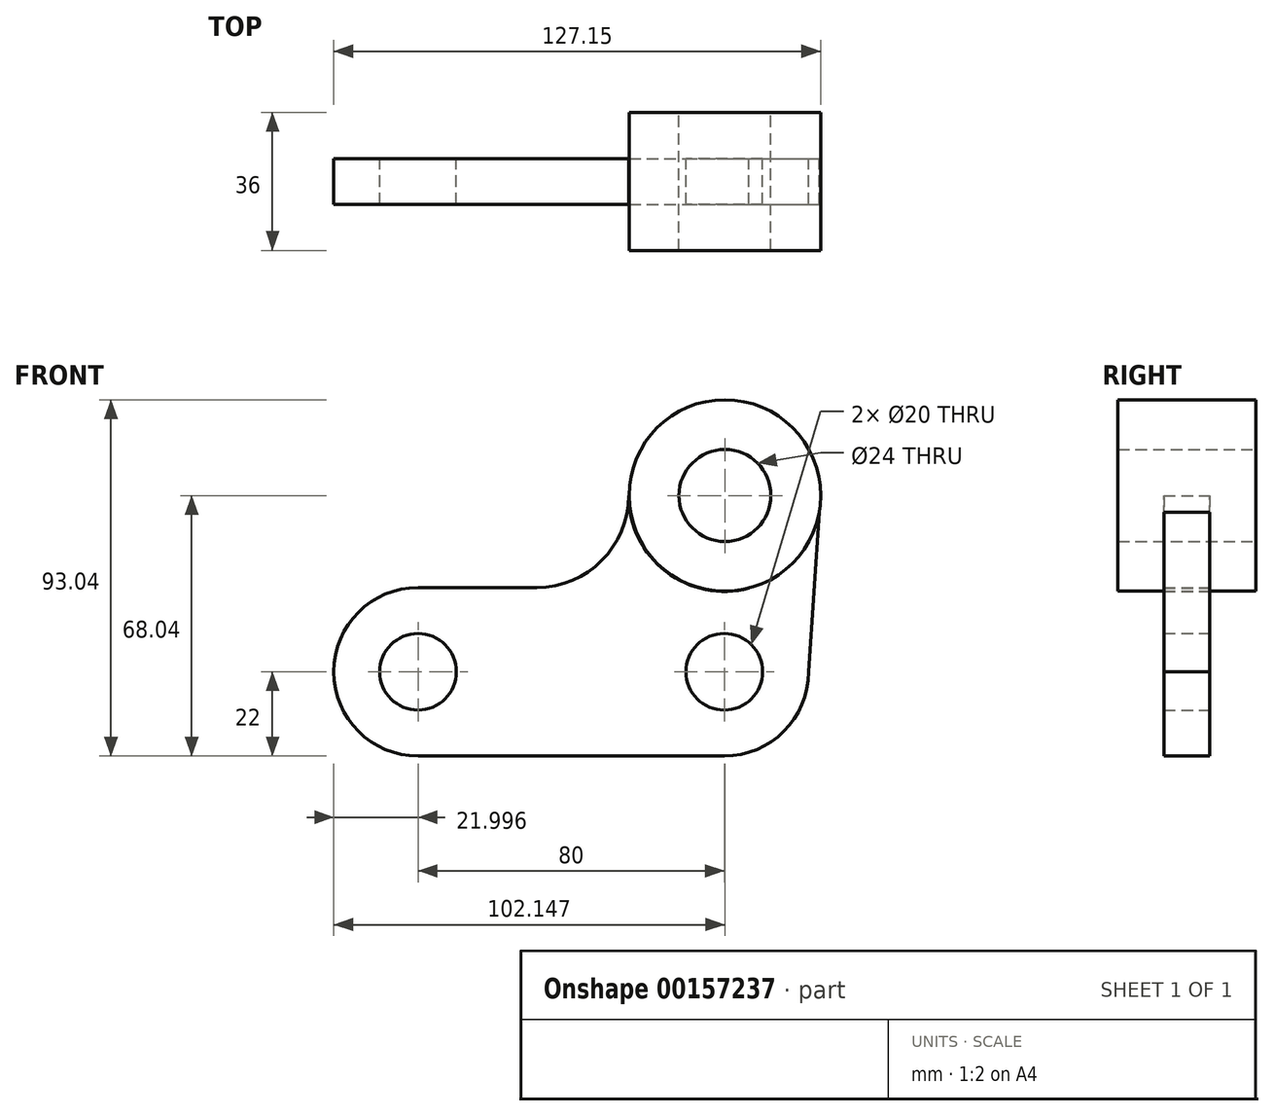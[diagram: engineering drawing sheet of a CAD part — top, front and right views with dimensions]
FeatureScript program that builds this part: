
annotation { "Feature Type Name" : "Feature", "Feature Type Description" : "" }
export const myFeature = defineFeature(function(context is Context, id is Id, definition is map)
    precondition{}
    {
        {
            var Q0;
            Q0=qCreatedBy(makeId("Front.planeOp"),FACE);
            var sketch = newSketch(context, id + "F0", { "sketchPlane" : qUnion([Q0])});
            skLineSegment(sketch, "E0", {"start": v(0, 0) * mm, "end": v(41.58, 0) * mm, "construction": true});
            skLineSegment(sketch, "E1", {"start": v(41.58, 0) * mm, "end": v(-38.42, 0) * mm, "construction": true});
            skCircle(sketch, "E2", {"center": v(-38.42, 0) * mm, "radius": 10 * mm});
            skCircle(sketch, "E3", {"center": v(41.58, 0) * mm, "radius": 10 * mm});
            skArc(sketch, "E4", {"start": v(-38.42, 22) * mm, "mid": v(-60.42, 0) * mm, "end": v(-38.42, -22) * mm});
            skArc(sketch, "E5", {"start": v(41.58, -22) * mm, "mid": v(57.13, -15.56) * mm, "end": v(63.58, 0) * mm});
            skLineSegment(sketch, "E6", {"start": v(41.58, 0) * mm, "end": v(41.58, 46) * mm, "construction": true});
            skCircle(sketch, "E7", {"center": v(41.58, 46) * mm, "radius": 25 * mm});
            skCircle(sketch, "E8", {"center": v(41.58, 46) * mm, "radius": 12 * mm});
            skLineSegment(sketch, "E9", {"start": v(16.58, 46) * mm, "end": v(16.58, 22) * mm});
            skLineSegment(sketch, "E10", {"start": v(16.58, 22) * mm, "end": v(-38.42, 22) * mm});
            skLineSegment(sketch, "E11", {"start": v(-38.42, -22) * mm, "end": v(41.58, -22) * mm});
            skLineSegment(sketch, "E12", {"start": v(63.58, 0) * mm, "end": v(66.52, 44.34) * mm});
            skSolve(sketch);
        }
        {
            var Q0;
            Q0=makeQuery(id+"F0.imprint","IMPRINT",FACE,{"disambiguationData":[TD([[makeQuery(id+"F0.imprint","IMPRINT",EDGE,{"derivedFrom":sQuery(id+"F0.wireOp",EDGE,"E2")}),-1.0]])]});
            extrude(context, id + "F1", {"entities" : qUnion([Q0]), "endBound" : BoundingType.SYMMETRIC, "depth" : 12 * mm});
        }
        {
            var Q0;
            Q0=qCreatedBy(makeId("Front.planeOp"),FACE);
            var sketch = newSketch(context, id + "F2", { "sketchPlane" : qUnion([Q0])});
            skPoint(sketch, "E13.first.point", {"position": v(41.5, 21.04) * mm});
            skPoint(sketch, "E13.second.point", {"position": v(15.05, 45.36) * mm});
            skPoint(sketch, "E13.third.point", {"position": v(66.66, 44.24) * mm});
            skCircle(sketch, "E14", {"center": v(41.73, 46.04) * mm, "radius": 25 * mm});
            skPoint(sketch, "E14.third.point", {"position": v(16.73, 45.99) * mm});
            skCircle(sketch, "E15", {"center": v(41.73, 46.04) * mm, "radius": 12 * mm});
            skPoint(sketch, "E16.center.orphan", {"position": v(0, 46.21) * mm});
            skSolve(sketch);
        }
        {
            var Q0;
            Q0=makeQuery(id+"F2.imprint","IMPRINT",FACE,{"disambiguationData":[TD([[makeQuery(id+"F2.imprint","IMPRINT",EDGE,{"derivedFrom":sQuery(id+"F2.wireOp",EDGE,"E14")}),1.0]])]});
            extrude(context, id + "F3", {"entities" : qUnion([Q0]), "operationType" : NewBodyOperationType.ADD, "endBound" : BoundingType.SYMMETRIC, "depth" : 36 * mm});
        }
        {
            var Q0;
            Q0=makeQuery(id+"F1.opExtrude","SWEPT_EDGE",EDGE,{"disambiguationData":[OSD([sQuery(id+"F0.wireOp",EDGE,"E9"),sQuery(id+"F0.wireOp",EDGE,"E10")])]});
            fillet(context, id + "F4", {"entities" : qUnion([Q0]), "radius" : 24 * mm, "tangentPropagation" : true, "allowEdgeOverflow" : false});
        }
    });
